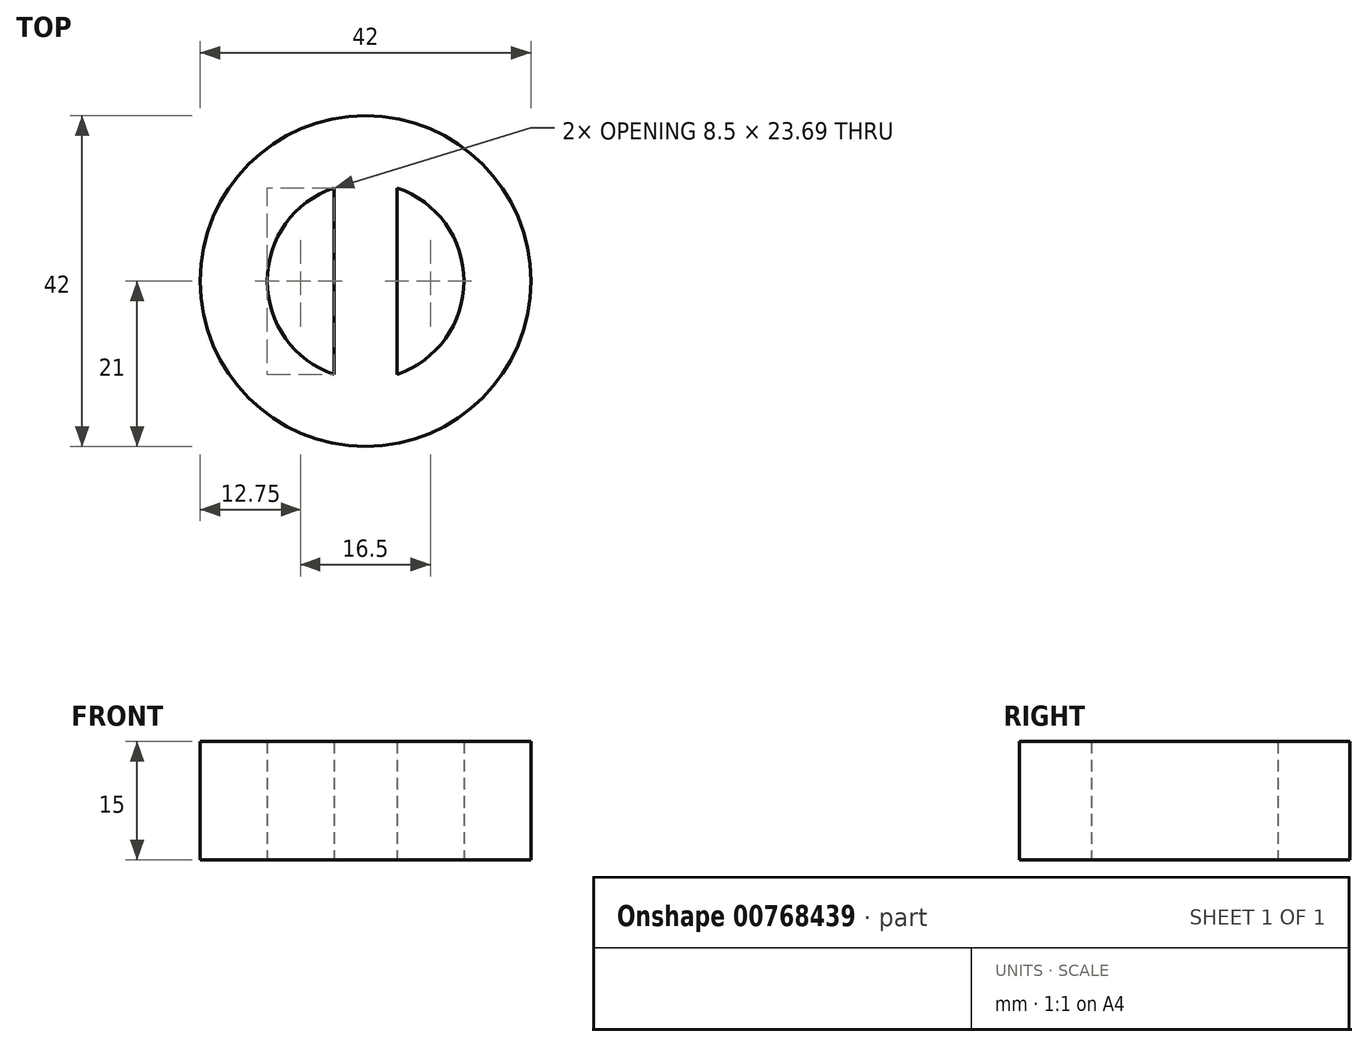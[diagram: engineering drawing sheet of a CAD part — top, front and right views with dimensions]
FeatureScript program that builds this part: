
annotation { "Feature Type Name" : "Feature", "Feature Type Description" : "" }
export const myFeature = defineFeature(function(context is Context, id is Id, definition is map)
    precondition{}
    {
        {
            var Q0;
            Q0=qCreatedBy(makeId("Top.planeOp"),FACE);
            var sketch = newSketch(context, id + "F0", { "sketchPlane" : qUnion([Q0])});
            skCircle(sketch, "E0", {"center": v(0, 0) * mm, "radius": 21 * mm});
            skArc(sketch, "E1", {"start": v(-4, 11.84) * mm, "mid": v(-12.5, 0) * mm, "end": v(-4, -11.84) * mm});
            skLineSegment(sketch, "E2.left", {"start": v(-4, 11.84) * mm, "end": v(-4, -11.84) * mm});
            skLineSegment(sketch, "E2.right", {"start": v(4, 11.84) * mm, "end": v(4, -11.84) * mm});
            skArc(sketch, "E3.trimOffspring", {"start": v(4, -11.84) * mm, "mid": v(12.5, 0) * mm, "end": v(4, 11.84) * mm});
            skSolve(sketch);
        }
        {
            var Q0;
            Q0 = qSketchRegion(id + "F0", true);
            extrude(context, id + "F1", {"entities" : qUnion([Q0]), "depth" : 15 * mm, "offsetDistance" : 25 * mm});
        }
    });
